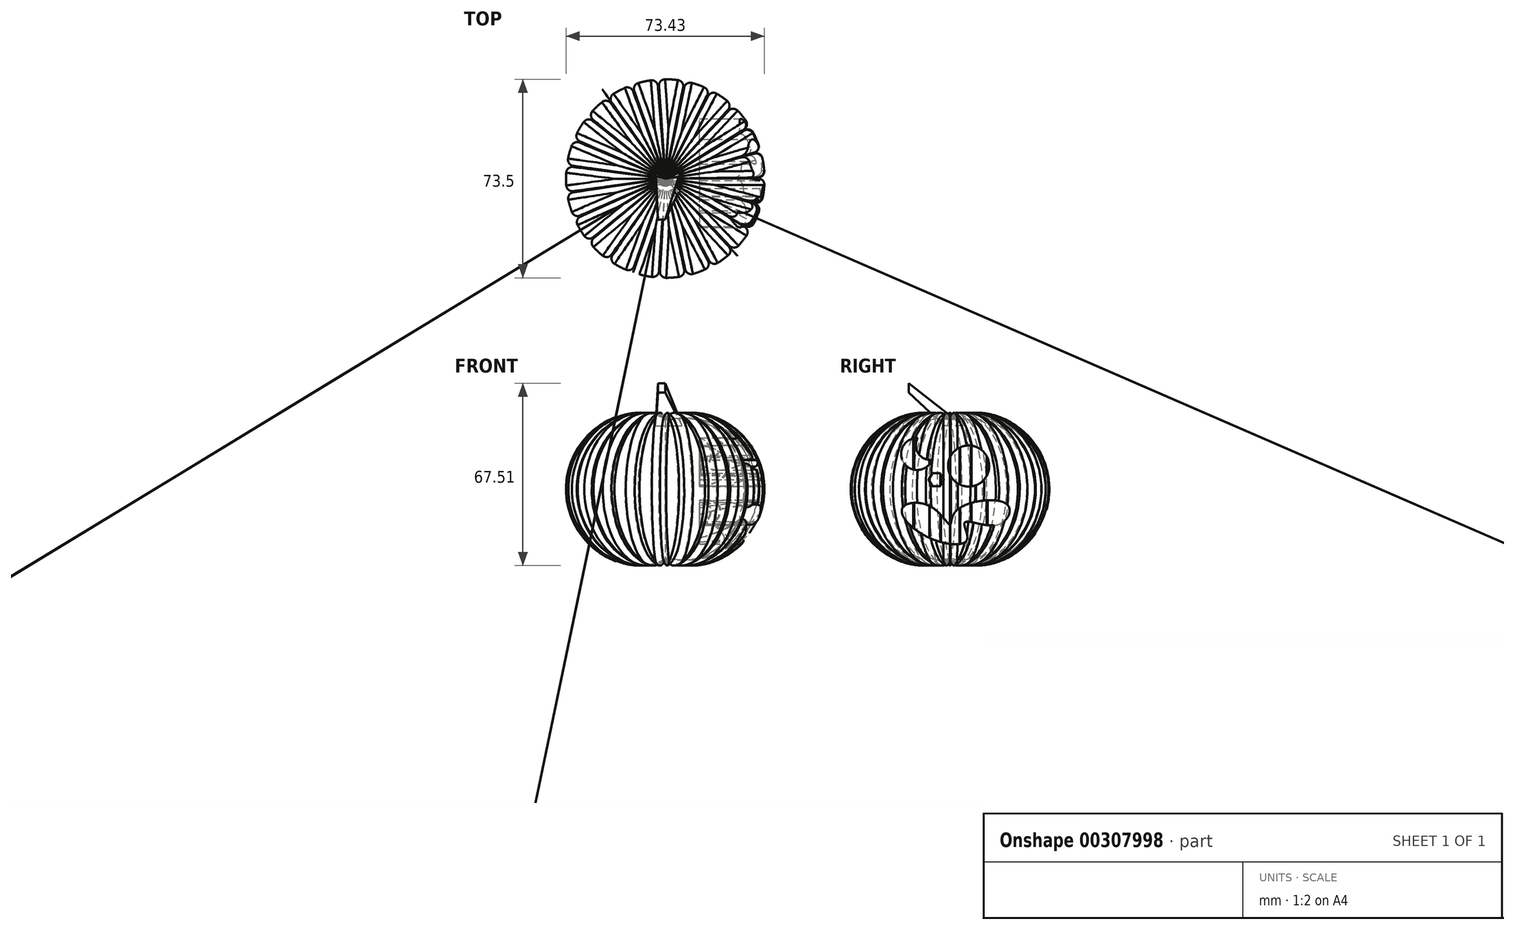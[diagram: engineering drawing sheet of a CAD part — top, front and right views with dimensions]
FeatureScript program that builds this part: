
annotation { "Feature Type Name" : "Feature", "Feature Type Description" : "" }
export const myFeature = defineFeature(function(context is Context, id is Id, definition is map)
    precondition{}
    {
        {
            var Q0;
            Q0=qCreatedBy(makeId("Front.planeOp"),FACE);
            var sketch = newSketch(context, id + "F0", { "sketchPlane" : qUnion([Q0])});
            skArc(sketch, "E0", {"start": v(0, 0) * mm, "mid": v(36.75, 27.38) * mm, "end": v(0, 54.76) * mm});
            skLineSegment(sketch, "E1", {"start": v(0, 54.76) * mm, "end": v(0, 0) * mm});
            skSolve(sketch);
        }
        {
            var Q0;
            Q0=makeQuery(id+"F0.imprint","IMPRINT",FACE,{"disambiguationData":[TD([[makeQuery(id+"F0.imprint","IMPRINT",EDGE,{"derivedFrom":sQuery(id+"F0.wireOp",EDGE,"E0")}),1.0]])]});
            var Q1;
            Q1=sQuery(id+"F0.wireOp",EDGE,"E1");
            revolve(context, id + "F1", {"entities" : qUnion([Q0]), "axis" : qUnion([Q1]), "revolveType" : RevolveType.ONE_DIRECTION, "angle" : 15 * degree});
        }
        {
            var Q0;
            Q0=makeQuery(id+"F1.opRevolve","CAP_EDGE",EDGE,{"disambiguationData":[OSD([sQuery(id+"F0.wireOp",EDGE,"E0")])],"isStart":false});
            var Q1;
            Q1=makeQuery(id+"F1.opRevolve","CAP_EDGE",EDGE,{"disambiguationData":[OSD([sQuery(id+"F0.wireOp",EDGE,"E0")])],"isStart":true});
            fillet(context, id + "F2", {"entities" : qUnion([Q0, Q1]), "radius" : 2.3 * mm, "tangentPropagation" : true, "allowEdgeOverflow" : false});
        }
        {
            var Q0;
            Q0=qCreatedBy(makeId("Top.planeOp"),FACE);
            cPlane(context, id + "F3", {"entities" : qUnion([Q0]), "cplaneType" : CPlaneType.OFFSET, "offset" : 50.8 * mm, "width" : 152.4 * mm, "height" : 152.4 * mm});
        }
        {
            var Q0;
            Q0=makeQuery(id+"F1.opRevolve","SWEPT_BODY",BODY,{"disambiguationData":[OSD([sQuery(id+"F0.wireOp",EDGE,"E0"),sQuery(id+"F0.wireOp",EDGE,"E1")])]});
            var Q1;
            Q1=makeQuery(id+"F1.opRevolve","CAP_EDGE",EDGE,{"disambiguationData":[OSD([sQuery(id+"F0.wireOp",EDGE,"E1")])],"isStart":true});
            circularPattern(context, id + "F4", {"entities" : qUnion([Q0]), "axis" : qUnion([Q1]), "angle" : 360 * degree, "instanceCount" : 23, "equalSpace" : true});
        }
        {
            var Q0;
            Q0=qCreatedBy(makeId("Front.planeOp"),FACE);
            cPlane(context, id + "F5", {"entities" : qUnion([Q0]), "cplaneType" : CPlaneType.OFFSET, "offset" : 15.24 * mm, "width" : 152.4 * mm, "height" : 152.4 * mm});
        }
        {
            var Q0;
            Q0=qCreatedBy(id+"F3.planeOp",FACE);
            var sketch = newSketch(context, id + "F6", { "sketchPlane" : qUnion([Q0])});
            skLineSegment(sketch, "E2.bottom", {"start": v(-3.58, 4.92) * mm, "end": v(6.26, 4.92) * mm});
            skLineSegment(sketch, "E2.top", {"start": v(-3.58, -2.23) * mm, "end": v(6.26, -2.23) * mm});
            skLineSegment(sketch, "E2.left", {"start": v(-3.58, 4.92) * mm, "end": v(-3.58, -2.23) * mm});
            skLineSegment(sketch, "E2.right", {"start": v(6.26, 4.92) * mm, "end": v(6.26, -2.23) * mm});
            skSolve(sketch);
        }
        {
            var Q0;
            Q0=qCreatedBy(id+"F5.planeOp",FACE);
            var sketch = newSketch(context, id + "F7", { "sketchPlane" : qUnion([Q0])});
            skLineSegment(sketch, "E3.bottom", {"start": v(-2.64, 66.6) * mm, "end": v(0, 66.6) * mm});
            skLineSegment(sketch, "E3.top", {"start": v(-2.64, 63.16) * mm, "end": v(0, 63.16) * mm});
            skLineSegment(sketch, "E3.left", {"start": v(-2.64, 66.6) * mm, "end": v(-2.64, 63.16) * mm});
            skLineSegment(sketch, "E3.right", {"start": v(0, 66.6) * mm, "end": v(0, 63.16) * mm});
            skSolve(sketch);
        }
        {
            var Q0;
            Q0 = qSketchRegion(id + "F6", true);
            var Q1;
            Q1 = qSketchRegion(id + "F7", true);
            loft(context, id + "F8", {"sheetProfilesArray" : [{ "sheetProfileEntities" : qUnion([Q0]) }, { "sheetProfileEntities" : qUnion([Q1]) }]});
        }
        {
            var Q0;
            Q0=qCreatedBy(makeId("Right.planeOp"),FACE);
            cPlane(context, id + "F9", {"entities" : qUnion([Q0]), "cplaneType" : CPlaneType.OFFSET, "offset" : 38.1 * mm, "width" : 152.4 * mm, "height" : 152.4 * mm});
        }
        {
            var Q0;
            Q0=qCreatedBy(id+"F9.planeOp",FACE);
            var sketch = newSketch(context, id + "F10", { "sketchPlane" : qUnion([Q0])});
            skCircle(sketch, "E4", {"center": v(-12.18, 40.41) * mm, "radius": 5.93 * mm});
            skCircle(sketch, "E5", {"center": v(6.9, 35.94) * mm, "radius": 7.6 * mm});
            skCircle(sketch, "E6", {"center": v(-7.2, 43.64) * mm, "radius": 5.46 * mm});
            skSolve(sketch);
        }
        {
            var Q0;
            Q0=qCreatedBy(id+"F9.planeOp",FACE);
            var sketch = newSketch(context, id + "F11", { "sketchPlane" : qUnion([Q0])});
            skFitSpline(sketch, "E7", {"points": [v(-17.67, 20.3) * mm, v(-8.53, 9.75) * mm, v(6.3, 8.73) * mm, v(5.48, 15.03) * mm, v(17.67, 14.21) * mm, v(21.32, 21.53) * mm, v(2.23, 19.3) * mm, v(0, 14.21) * mm, v(-7.1, 20.92) * mm, v(-17.67, 20.3) * mm]});
            skCircle(sketch, "E8.cCircle", {"center": v(-5.08, 30.87) * mm, "radius": 2.44 * mm, "construction": true});
            skLineSegment(sketch, "E8.0", {"start": v(-3.67, 28.43) * mm, "end": v(-6.48, 28.43) * mm});
            skLineSegment(sketch, "E8.1", {"start": v(-6.48, 28.43) * mm, "end": v(-7.9, 30.87) * mm});
            skLineSegment(sketch, "E8.2", {"start": v(-7.9, 30.87) * mm, "end": v(-6.48, 33.3) * mm});
            skLineSegment(sketch, "E8.3", {"start": v(-6.48, 33.3) * mm, "end": v(-3.67, 33.3) * mm});
            skLineSegment(sketch, "E8.4", {"start": v(-3.67, 33.3) * mm, "end": v(-2.26, 30.87) * mm});
            skLineSegment(sketch, "E8.5", {"start": v(-2.26, 30.87) * mm, "end": v(-3.67, 28.43) * mm});
            skPoint(sketch, "E8.0.midPoint", {"position": v(-5.08, 28.43) * mm});
            skSolve(sketch);
        }
        {
            var Q0;
            {var subQ0=sQuery(id+"F10.wireOp",EDGE,"E6");var subQ1=sQuery(id+"F10.wireOp",EDGE,"E4");var subQ2=makeQuery(id+"F10.imprint","INTERSECT",VERTEX,{"disambiguationData":[OD(0.0)],"derivedFrom":[subQ1,subQ0]});Q0=makeQuery(id+"F10.imprint","IMPRINT",FACE,{"disambiguationData":[TD([[makeQuery(id+"F10.imprint","IMPRINT",EDGE,{"disambiguationData":[TD([[subQ2,1.0]])],"derivedFrom":subQ1}),1.0]])]});}
            var Q1;
            Q1=makeQuery(id+"F10.imprint","IMPRINT",FACE,{"disambiguationData":[TD([[makeQuery(id+"F10.imprint","IMPRINT",EDGE,{"derivedFrom":sQuery(id+"F10.wireOp",EDGE,"E5")}),1.0]])]});
            var Q2;
            Q2=makeQuery(id+"F11.imprint","IMPRINT",FACE,{"disambiguationData":[TD([[makeQuery(id+"F11.imprint","IMPRINT",EDGE,{"derivedFrom":sQuery(id+"F11.wireOp",EDGE,"E7")}),1.0]])]});
            var Q3;
            Q3=makeQuery(id+"F11.imprint","IMPRINT",FACE,{"disambiguationData":[TD([[makeQuery(id+"F11.imprint","IMPRINT",EDGE,{"derivedFrom":sQuery(id+"F11.wireOp",EDGE,"E8.0")}),-1.0]])]});
            extrude(context, id + "F12", {"entities" : qUnion([Q0, Q1, Q2, Q3]), "operationType" : NewBodyOperationType.REMOVE, "oppositeDirection" : true, "depth" : 25.4 * mm});
        }
    });
